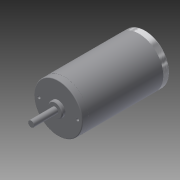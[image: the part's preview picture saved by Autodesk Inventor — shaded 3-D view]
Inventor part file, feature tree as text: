
AUTODESK INVENTOR PART (.ipt)
format: ipt  version: 2014 SP1 (Build 180222100, 222)  size: 142,336 bytes
history: native  units: in
note: dims shown in document units (in); Inventor stores cm internally (conversion verified against a paired STEP export)
features: fillet x1, other x1, imported_body x1
ambient origin geometry x8: Origin, YZ Plane, XZ Plane, XY Plane, X Axis, Y Axis, Z Axis, Center Point
bodies: Body1 (feature_tree)
feature tree (3):
  fillet  "Fillet4"  [1 undecoded]
  other  "CIM Motor SW.ipt1"
  imported_body  "Base1"
note: 1 required parameter value undecoded (feature->parameter linkage not recoverable at this tier; creation-order binding heuristic only, values carry confidence <= 0.55)
